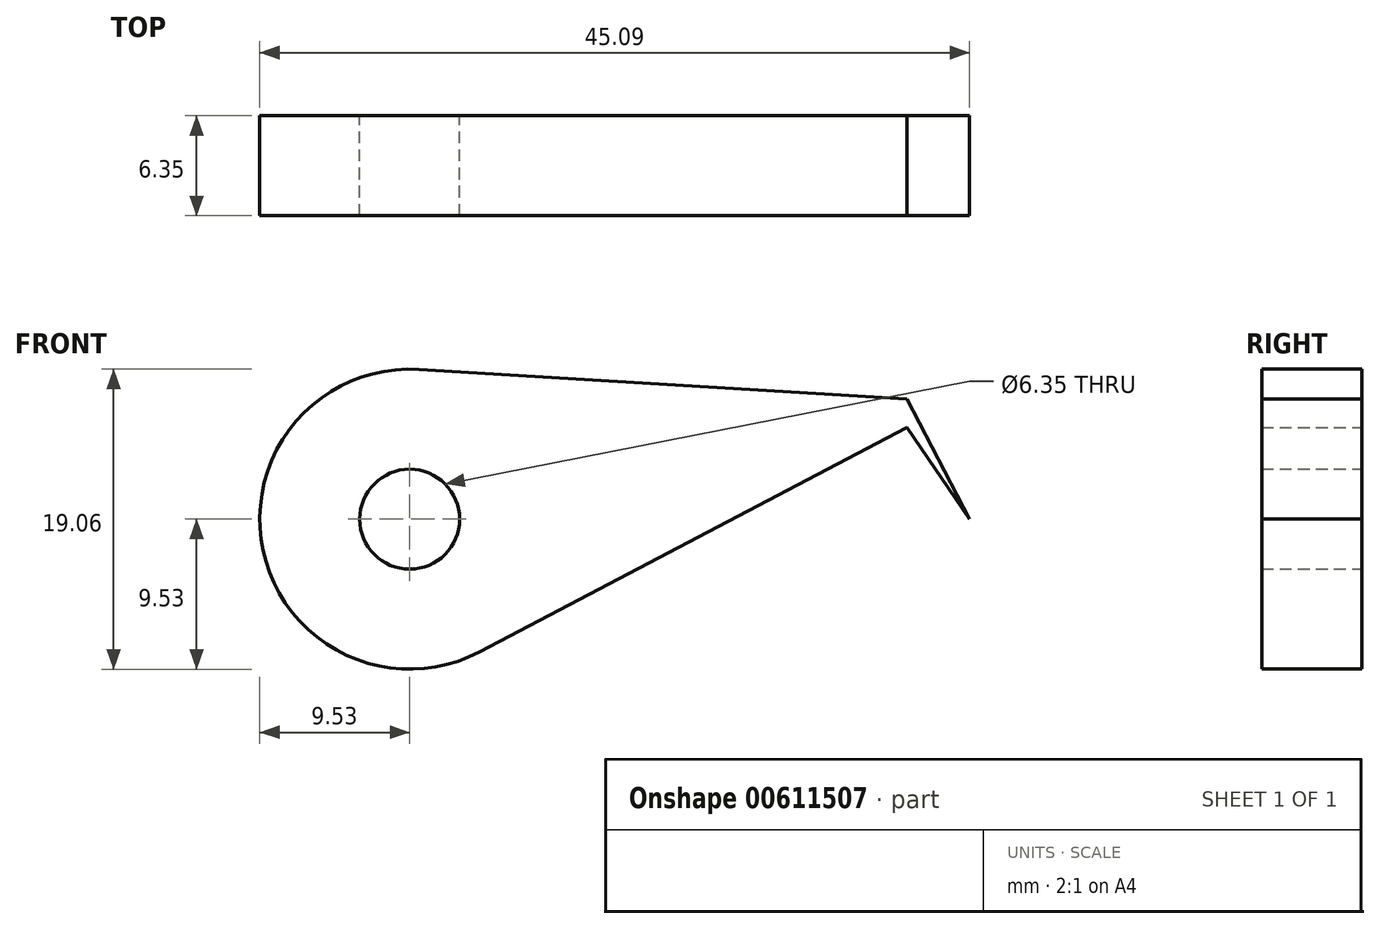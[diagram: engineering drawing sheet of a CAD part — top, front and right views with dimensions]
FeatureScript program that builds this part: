
annotation { "Feature Type Name" : "Feature", "Feature Type Description" : "" }
export const myFeature = defineFeature(function(context is Context, id is Id, definition is map)
    precondition{}
    {
        {
            var Q0;
            Q0=qCreatedBy(makeId("Front.planeOp"),FACE);
            var sketch = newSketch(context, id + "F0", { "sketchPlane" : qUnion([Q0])});
            skCircle(sketch, "E0", {"center": v(0, 0) * mm, "radius": 3.18 * mm});
            skCircle(sketch, "E1", {"center": v(0, 0) * mm, "radius": 9.53 * mm});
            skLineSegment(sketch, "E2", {"start": v(0.58, 9.5) * mm, "end": v(31.58, 7.62) * mm});
            skLineSegment(sketch, "E3", {"start": v(31.58, 7.62) * mm, "end": v(30.67, 7.68) * mm});
            skLineSegment(sketch, "E4", {"start": v(4.43, -8.43) * mm, "end": v(20.48, 0) * mm});
            skLineSegment(sketch, "E5", {"start": v(20.48, 0) * mm, "end": v(31.58, 5.83) * mm});
            skLineSegment(sketch, "E6", {"start": v(31.58, 5.83) * mm, "end": v(35.56, 0) * mm});
            skLineSegment(sketch, "E7", {"start": v(35.56, 0) * mm, "end": v(31.58, 7.62) * mm});
            skSolve(sketch);
        }
        {
            var Q0;
            Q0 = qSketchRegion(id + "F0", true);
            extrude(context, id + "F1", {"entities" : qUnion([Q0]), "depth" : 6.35 * mm, "offsetDistance" : 25.4 * mm});
        }
        {
            var Q0;
            Q0 = qSketchRegion(id + "Fn6BFYUFTjKjm5v_1", true);
            var Q1;
            Q1=sQuery(id+"F0.wireOp",EDGE,"E0");
            extrude(context, id + "F2", {"entities" : qUnion([Q0]), "bodyType" : ToolBodyType.SURFACE, "surfaceEntities" : qUnion([Q1]), "oppositeDirection" : true, "depth" : 6.35 * mm, "offsetDistance" : 25.4 * mm});
        }
    });
